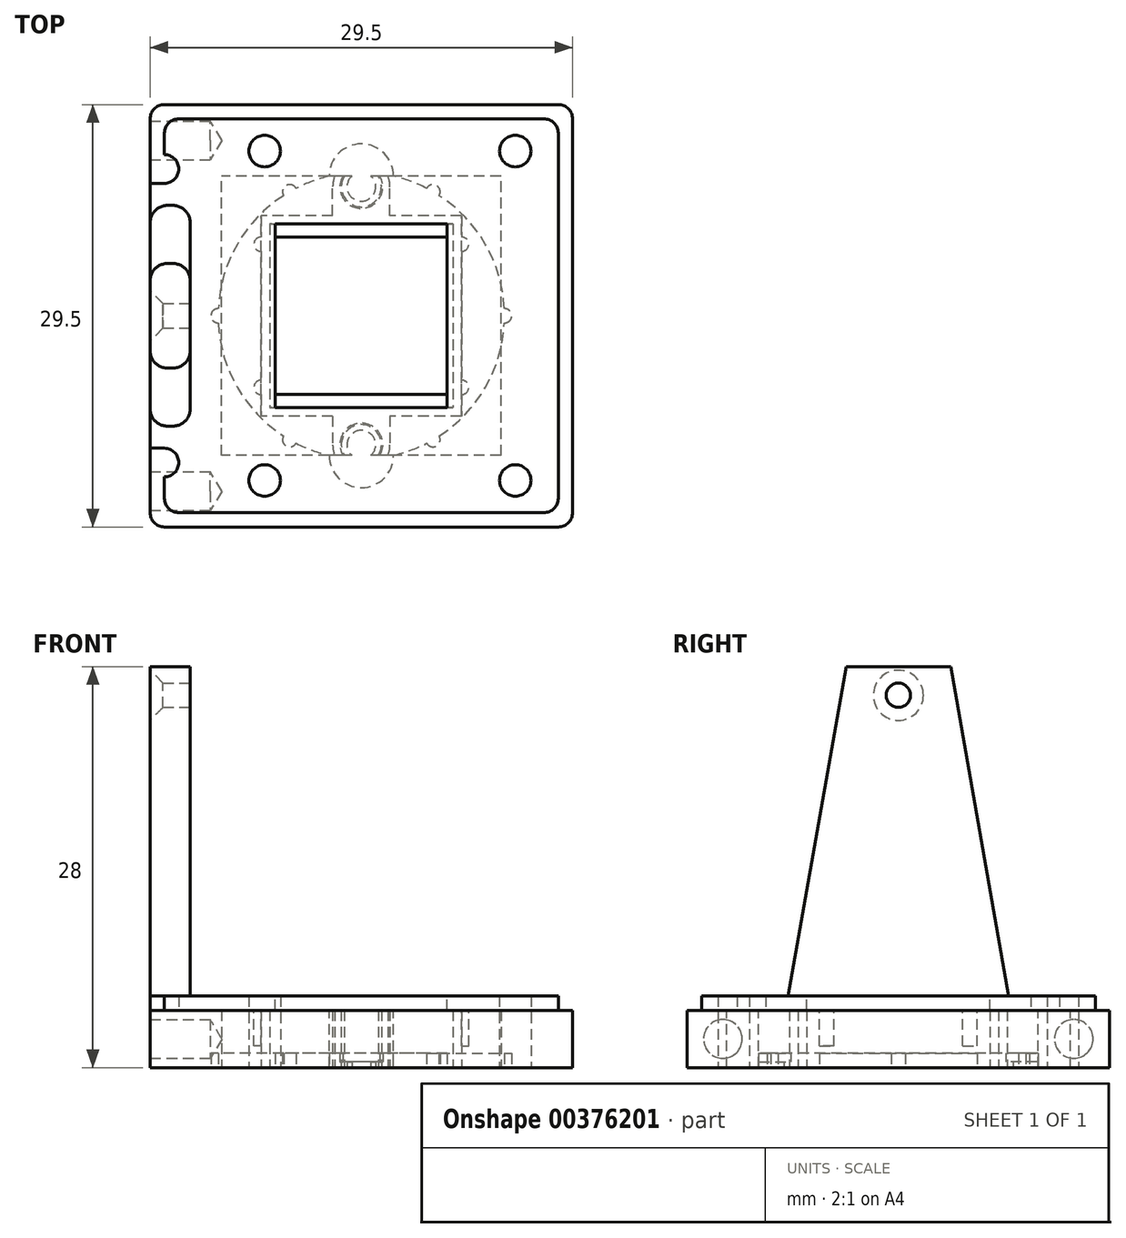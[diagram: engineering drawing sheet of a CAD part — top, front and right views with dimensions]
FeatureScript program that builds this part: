
annotation { "Feature Type Name" : "Feature", "Feature Type Description" : "" }
export const myFeature = defineFeature(function(context is Context, id is Id, definition is map)
    precondition{}
    {
        {
            var Q0;
            Q0=qCreatedBy(makeId("Top.planeOp"),FACE);
            var sketch = newSketch(context, id + "F0", { "sketchPlane" : qUnion([Q0])});
            skLineSegment(sketch, "E0.bottom", {"start": v(14.75, -14.75) * mm, "end": v(-14.75, -14.75) * mm});
            skLineSegment(sketch, "E0.top", {"start": v(14.75, 14.75) * mm, "end": v(-14.75, 14.75) * mm});
            skLineSegment(sketch, "E0.left", {"start": v(14.75, -14.75) * mm, "end": v(14.75, 14.75) * mm});
            skLineSegment(sketch, "E0.right", {"start": v(-14.75, -14.75) * mm, "end": v(-14.75, 14.75) * mm});
            skPoint(sketch, "E0.middle", {"position": v(0, 0) * mm});
            skLineSegment(sketch, "E1.0", {"start": v(-9.75, -9.75) * mm, "end": v(-9.75, 9.75) * mm});
            skLineSegment(sketch, "E1.1", {"start": v(9.75, -9.75) * mm, "end": v(-9.75, -9.75) * mm});
            skLineSegment(sketch, "E1.2", {"start": v(9.75, -9.75) * mm, "end": v(9.75, 9.75) * mm});
            skLineSegment(sketch, "E1.3", {"start": v(9.75, 9.75) * mm, "end": v(-9.75, 9.75) * mm});
            skSolve(sketch);
        }
        {
            var Q0;
            Q0=qSketchRegion(id+"F0",true);
            extrude(context, id + "F1", {"entities" : qUnion([Q0]), "depth" : 4 * mm, "offsetDistance" : 25 * mm});
        }
        {
            var Q0;
            Q0=makeQuery(id+"F1.opExtrude","CAP_FACE",FACE,{"disambiguationData":[OSD([sQuery(id+"F0.wireOp",EDGE,"E0.bottom"),sQuery(id+"F0.wireOp",EDGE,"E0.top"),sQuery(id+"F0.wireOp",EDGE,"E0.left"),sQuery(id+"F0.wireOp",EDGE,"E0.right"),sQuery(id+"F0.wireOp",EDGE,"E1.0"),sQuery(id+"F0.wireOp",EDGE,"E1.1"),sQuery(id+"F0.wireOp",EDGE,"E1.2"),sQuery(id+"F0.wireOp",EDGE,"E1.3")])],"isStart":false});
            var sketch = newSketch(context, id + "F2", { "sketchPlane" : qUnion([Q0])});
            skLineSegment(sketch, "E2.0", {"start": v(13.75, 13.75) * mm, "end": v(-13.75, 13.75) * mm});
            skLineSegment(sketch, "E2.1", {"start": v(13.75, -13.75) * mm, "end": v(13.75, 13.75) * mm});
            skLineSegment(sketch, "E2.2", {"start": v(13.75, -13.75) * mm, "end": v(-13.75, -13.75) * mm});
            skLineSegment(sketch, "E2.3", {"start": v(-13.75, -13.75) * mm, "end": v(-13.75, -11.25) * mm});
            skLineSegment(sketch, "E3.bottom", {"start": v(-14.75, -8.65) * mm, "end": v(-11.95, -8.65) * mm});
            skLineSegment(sketch, "E3.top", {"start": v(-14.75, 8.65) * mm, "end": v(-11.95, 8.65) * mm});
            skLineSegment(sketch, "E3.left", {"start": v(-14.75, -8.65) * mm, "end": v(-14.75, 8.65) * mm});
            skLineSegment(sketch, "E3.right", {"start": v(-11.95, -8.65) * mm, "end": v(-11.95, 8.65) * mm});
            skPoint(sketch, "E3.middle", {"position": v(-13.35, 0) * mm});
            skPoint(sketch, "E3.middle.positionSnap0", {"position": v(-13.75, 0) * mm});
            skPoint(sketch, "E3.centerSnap0", {"position": v(-13.75, 0) * mm});
            skLineSegment(sketch, "E4.trimOffspring", {"start": v(-13.75, 11.25) * mm, "end": v(-13.75, 13.75) * mm});
            skArc(sketch, "E5", {"start": v(-13.75, 9.25) * mm, "mid": v(-12.75, 10.25) * mm, "end": v(-13.75, 11.25) * mm});
            skArc(sketch, "E6", {"start": v(-13.75, -11.25) * mm, "mid": v(-12.75, -10.25) * mm, "end": v(-13.75, -9.25) * mm});
            skLineSegment(sketch, "E7", {"start": v(-13.75, -9.25) * mm, "end": v(-14.75, -9.25) * mm});
            skLineSegment(sketch, "E8", {"start": v(-13.75, 9.25) * mm, "end": v(-14.75, 9.25) * mm});
            skCircle(sketch, "E9", {"center": v(0, 9.75) * mm, "radius": 2.25 * mm});
            skCircle(sketch, "E10", {"center": v(0, -9.75) * mm, "radius": 2.25 * mm});
            skCircle(sketch, "E11", {"center": v(0, 9.75) * mm, "radius": 1.25 * mm, "construction": true});
            skCircle(sketch, "E12", {"center": v(0, -9.75) * mm, "radius": 1.25 * mm, "construction": true});
            skLineSegment(sketch, "E13", {"start": v(-13.35, 0) * mm, "end": v(0, 0) * mm, "construction": true});
            skLineSegment(sketch, "E14.bottom", {"start": v(6, -7) * mm, "end": v(-6, -7) * mm});
            skLineSegment(sketch, "E14.top", {"start": v(6, 7) * mm, "end": v(-6, 7) * mm});
            skLineSegment(sketch, "E14.left", {"start": v(6, -7) * mm, "end": v(6, 7) * mm});
            skLineSegment(sketch, "E14.right", {"start": v(-6, -7) * mm, "end": v(-6, 7) * mm});
            skPoint(sketch, "E14.middle", {"position": v(0, 0) * mm});
            skSolve(sketch);
        }
        {
            var Q0;
            {var subQ5=sQuery(id+"F2.wireOp",EDGE,"E8");Q0=makeQuery(id+"F2.imprint","IMPRINT",FACE,{"disambiguationData":[TD([[makeQuery(id+"F2.imprint","IMPRINT",EDGE,{"derivedFrom":subQ5}),1.0]])]});}
            var Q1;
            {var subQ8=sQuery(id+"F2.wireOp",EDGE,"E2.0");Q1=makeQuery(id+"F2.imprint","IMPRINT",FACE,{"disambiguationData":[TD([[makeQuery(id+"F2.imprint","IMPRINT",EDGE,{"derivedFrom":subQ8}),1.0]])]});}
            var Q2;
            {var subQ3=sQuery(id+"F2.wireOp",EDGE,"E7");Q2=makeQuery(id+"F2.imprint","IMPRINT",FACE,{"disambiguationData":[TD([[makeQuery(id+"F2.imprint","IMPRINT",EDGE,{"derivedFrom":subQ3}),-1.0]])]});}
            var Q3;
            {var subQ3=sQuery(id+"F2.wireOp",EDGE,"E3.left");Q3=makeQuery(id+"F2.imprint","IMPRINT",FACE,{"disambiguationData":[TD([[makeQuery(id+"F2.imprint","IMPRINT",EDGE,{"derivedFrom":subQ3}),-1.0]])]});}
            var Q4;
            Q4=makeQuery(id+"F2.imprint","IMPRINT",FACE,{"disambiguationData":[TD([[makeQuery(id+"F2.imprint","IMPRINT",EDGE,{"derivedFrom":sQuery(id+"F2.wireOp",EDGE,"E14.bottom")}),1.0]])]});
            var Q5;
            {var subQ0=sQuery(id+"F2.wireOp",EDGE,"E9");var subQ1=makeQuery(id+"F1.opExtrude","CAP_EDGE",EDGE,{"disambiguationData":[OSD([sQuery(id+"F0.wireOp",EDGE,"E1.3")])],"isStart":false});var subQ2=makeQuery(id+"F2.imprint","INTERSECT",VERTEX,{"disambiguationData":[OD(0.0)],"derivedFrom":[subQ1,subQ0]});Q5=makeQuery(id+"F2.imprint","IMPRINT",FACE,{"disambiguationData":[TD([[makeQuery(id+"F2.imprint","IMPRINT",EDGE,{"disambiguationData":[TD([[subQ2,-1.0]])],"derivedFrom":subQ0}),1.0]])]});}
            var Q6;
            {var subQ0=sQuery(id+"F2.wireOp",EDGE,"E9");var subQ1=makeQuery(id+"F1.opExtrude","CAP_EDGE",EDGE,{"disambiguationData":[OSD([sQuery(id+"F0.wireOp",EDGE,"E1.3")])],"isStart":false});var subQ2=makeQuery(id+"F2.imprint","INTERSECT",VERTEX,{"disambiguationData":[OD(0.0)],"derivedFrom":[subQ1,subQ0]});Q6=makeQuery(id+"F2.imprint","IMPRINT",FACE,{"disambiguationData":[TD([[makeQuery(id+"F2.imprint","IMPRINT",EDGE,{"disambiguationData":[TD([[subQ2,1.0]])],"derivedFrom":subQ0}),1.0]])]});}
            var Q7;
            {var subQ0=sQuery(id+"F2.wireOp",EDGE,"E10");var subQ1=makeQuery(id+"F1.opExtrude","CAP_EDGE",EDGE,{"disambiguationData":[OSD([sQuery(id+"F0.wireOp",EDGE,"E1.1")])],"isStart":false});var subQ2=makeQuery(id+"F2.imprint","INTERSECT",VERTEX,{"disambiguationData":[OD(0.0)],"derivedFrom":[subQ1,subQ0]});Q7=makeQuery(id+"F2.imprint","IMPRINT",FACE,{"disambiguationData":[TD([[makeQuery(id+"F2.imprint","IMPRINT",EDGE,{"disambiguationData":[TD([[subQ2,-1.0]])],"derivedFrom":subQ0}),1.0]])]});}
            var Q8;
            {var subQ0=sQuery(id+"F2.wireOp",EDGE,"E10");var subQ1=makeQuery(id+"F1.opExtrude","CAP_EDGE",EDGE,{"disambiguationData":[OSD([sQuery(id+"F0.wireOp",EDGE,"E1.1")])],"isStart":false});var subQ2=makeQuery(id+"F2.imprint","INTERSECT",VERTEX,{"disambiguationData":[OD(0.0)],"derivedFrom":[subQ1,subQ0]});Q8=makeQuery(id+"F2.imprint","IMPRINT",FACE,{"disambiguationData":[TD([[makeQuery(id+"F2.imprint","IMPRINT",EDGE,{"disambiguationData":[TD([[subQ2,1.0]])],"derivedFrom":subQ0}),1.0]])]});}
            var Q9;
            {var subQ0=sQuery(id+"F2.wireOp",EDGE,"E12");var subQ1=makeQuery(id+"F1.opExtrude","CAP_EDGE",EDGE,{"disambiguationData":[OSD([sQuery(id+"F0.wireOp",EDGE,"E1.1")])],"isStart":false});var subQ2=makeQuery(id+"F2.imprint","INTERSECT",VERTEX,{"disambiguationData":[OD(0.0)],"derivedFrom":[subQ1,subQ0]});Q9=makeQuery(id+"F2.imprint","IMPRINT",FACE,{"disambiguationData":[TD([[makeQuery(id+"F2.imprint","IMPRINT",EDGE,{"disambiguationData":[TD([[subQ2,-1.0]])],"derivedFrom":subQ0}),1.0]])]});}
            var Q10;
            {var subQ0=sQuery(id+"F2.wireOp",EDGE,"E11");var subQ1=makeQuery(id+"F1.opExtrude","CAP_EDGE",EDGE,{"disambiguationData":[OSD([sQuery(id+"F0.wireOp",EDGE,"E1.3")])],"isStart":false});var subQ2=makeQuery(id+"F2.imprint","INTERSECT",VERTEX,{"disambiguationData":[OD(0.0)],"derivedFrom":[subQ1,subQ0]});Q10=makeQuery(id+"F2.imprint","IMPRINT",FACE,{"disambiguationData":[TD([[makeQuery(id+"F2.imprint","IMPRINT",EDGE,{"disambiguationData":[TD([[subQ2,-1.0]])],"derivedFrom":subQ0}),1.0]])]});}
            var Q11;
            {var subQ0=sQuery(id+"F2.wireOp",EDGE,"E11");var subQ1=makeQuery(id+"F1.opExtrude","CAP_EDGE",EDGE,{"disambiguationData":[OSD([sQuery(id+"F0.wireOp",EDGE,"E1.3")])],"isStart":false});var subQ2=makeQuery(id+"F2.imprint","INTERSECT",VERTEX,{"disambiguationData":[OD(0.0)],"derivedFrom":[subQ1,subQ0]});Q11=makeQuery(id+"F2.imprint","IMPRINT",FACE,{"disambiguationData":[TD([[makeQuery(id+"F2.imprint","IMPRINT",EDGE,{"disambiguationData":[TD([[subQ2,1.0]])],"derivedFrom":subQ0}),1.0]])]});}
            var Q12;
            {var subQ0=sQuery(id+"F2.wireOp",EDGE,"E12");var subQ1=makeQuery(id+"F1.opExtrude","CAP_EDGE",EDGE,{"disambiguationData":[OSD([sQuery(id+"F0.wireOp",EDGE,"E1.1")])],"isStart":false});var subQ2=makeQuery(id+"F2.imprint","INTERSECT",VERTEX,{"disambiguationData":[OD(0.0)],"derivedFrom":[subQ1,subQ0]});Q12=makeQuery(id+"F2.imprint","IMPRINT",FACE,{"disambiguationData":[TD([[makeQuery(id+"F2.imprint","IMPRINT",EDGE,{"disambiguationData":[TD([[subQ2,1.0]])],"derivedFrom":subQ0}),1.0]])]});}
            extrude(context, id + "F3", {"entities" : qUnion([Q0, Q1, Q2, Q3, Q4, Q5, Q6, Q7, Q8, Q9, Q10, Q11, Q12]), "operationType" : NewBodyOperationType.ADD, "depth" : 1 * mm, "offsetDistance" : 25 * mm});
        }
        {
            var Q0;
            {var subQ5=sQuery(id+"F2.wireOp",EDGE,"E3.left");Q0=makeQuery(id+"F2.imprint","IMPRINT",FACE,{"disambiguationData":[TD([[makeQuery(id+"F2.imprint","IMPRINT",EDGE,{"derivedFrom":subQ5}),-1.0]])]});}
            var Q1;
            {var subQ5=sQuery(id+"F2.wireOp",EDGE,"E3.right");Q1=makeQuery(id+"F2.imprint","IMPRINT",FACE,{"disambiguationData":[TD([[makeQuery(id+"F2.imprint","IMPRINT",EDGE,{"derivedFrom":subQ5}),1.0]])]});}
            extrude(context, id + "F4", {"entities" : qUnion([Q0, Q1]), "operationType" : NewBodyOperationType.ADD, "depth" : 24 * mm, "offsetDistance" : 25 * mm});
        }
        {
            var Q0;
            Q0=makeQuery(id+"F4.opExtrude","CAP_EDGE",EDGE,{"disambiguationData":[OSD([sQuery(id+"F2.wireOp",EDGE,"E3.bottom")])],"isStart":false});
            var Q1;
            Q1=makeQuery(id+"F4.opExtrude","CAP_EDGE",EDGE,{"disambiguationData":[OSD([sQuery(id+"F2.wireOp",EDGE,"E3.top")])],"isStart":false});
            chamfer(context, id + "F5", {"entities" : qUnion([Q0, Q1]), "chamferType" : ChamferType.OFFSET_ANGLE, "width" : 5 * mm, "oppositeDirection" : false, "angle" : 80 * degree, "tangentPropagation" : true});
        }
        {
            var Q0;
            Q0=makeQuery(id+"F5.opChamfer","BLEND_EDGE",EDGE,{"blendedFrom":[makeQuery(id+"F4.opExtrude","CAP_EDGE",EDGE,{"disambiguationData":[OSD([sQuery(id+"F2.wireOp",EDGE,"E3.bottom")])],"isStart":false}),makeQuery(id+"F4.opExtrude","SWEPT_FACE",FACE,{"disambiguationData":[OSD([sQuery(id+"F2.wireOp",EDGE,"E3.right")])]})],"blendedInto":[makeQuery(id+"F4.opExtrude","SWEPT_FACE",FACE,{"disambiguationData":[OSD([sQuery(id+"F2.wireOp",EDGE,"E3.right")])]})]});
            var Q1;
            Q1=makeQuery(id+"F5.opChamfer","BLEND_EDGE",EDGE,{"blendedFrom":[makeQuery(id+"F4.opExtrude","CAP_EDGE",EDGE,{"disambiguationData":[OSD([sQuery(id+"F2.wireOp",EDGE,"E3.bottom")])],"isStart":false}),makeQuery(id+"F4.boolean.opBoolean","MERGE",FACE,{"derivedFrom":[makeQuery(id+"F1.opExtrude","SWEPT_FACE",FACE,{"disambiguationData":[OSD([sQuery(id+"F0.wireOp",EDGE,"E0.right")])]}),makeQuery(id+"F4.opExtrude","SWEPT_FACE",FACE,{"disambiguationData":[OSD([sQuery(id+"F2.wireOp",EDGE,"E3.left")])]})]})],"blendedInto":[makeQuery(id+"F4.boolean.opBoolean","MERGE",FACE,{"derivedFrom":[makeQuery(id+"F1.opExtrude","SWEPT_FACE",FACE,{"disambiguationData":[OSD([sQuery(id+"F0.wireOp",EDGE,"E0.right")])]}),makeQuery(id+"F4.opExtrude","SWEPT_FACE",FACE,{"disambiguationData":[OSD([sQuery(id+"F2.wireOp",EDGE,"E3.left")])]})]})]});
            var Q2;
            Q2=makeQuery(id+"F5.opChamfer","BLEND_EDGE",EDGE,{"blendedFrom":[makeQuery(id+"F4.opExtrude","CAP_EDGE",EDGE,{"disambiguationData":[OSD([sQuery(id+"F2.wireOp",EDGE,"E3.top")])],"isStart":false}),makeQuery(id+"F4.opExtrude","SWEPT_FACE",FACE,{"disambiguationData":[OSD([sQuery(id+"F2.wireOp",EDGE,"E3.right")])]})],"blendedInto":[makeQuery(id+"F4.opExtrude","SWEPT_FACE",FACE,{"disambiguationData":[OSD([sQuery(id+"F2.wireOp",EDGE,"E3.right")])]})]});
            var Q3;
            Q3=makeQuery(id+"F5.opChamfer","BLEND_EDGE",EDGE,{"blendedFrom":[makeQuery(id+"F4.opExtrude","CAP_EDGE",EDGE,{"disambiguationData":[OSD([sQuery(id+"F2.wireOp",EDGE,"E3.top")])],"isStart":false}),makeQuery(id+"F4.boolean.opBoolean","MERGE",FACE,{"derivedFrom":[makeQuery(id+"F1.opExtrude","SWEPT_FACE",FACE,{"disambiguationData":[OSD([sQuery(id+"F0.wireOp",EDGE,"E0.right")])]}),makeQuery(id+"F4.opExtrude","SWEPT_FACE",FACE,{"disambiguationData":[OSD([sQuery(id+"F2.wireOp",EDGE,"E3.left")])]})]})],"blendedInto":[makeQuery(id+"F4.boolean.opBoolean","MERGE",FACE,{"derivedFrom":[makeQuery(id+"F1.opExtrude","SWEPT_FACE",FACE,{"disambiguationData":[OSD([sQuery(id+"F0.wireOp",EDGE,"E0.right")])]}),makeQuery(id+"F4.opExtrude","SWEPT_FACE",FACE,{"disambiguationData":[OSD([sQuery(id+"F2.wireOp",EDGE,"E3.left")])]})]})]});
            fillet(context, id + "F6", {"entities" : qUnion([Q0, Q1, Q2, Q3]), "radius" : 1.2 * mm, "tangentPropagation" : true, "allowEdgeOverflow" : false});
        }
        {
            var Q0;
            Q0=makeQuery(id+"F3.opExtrude","CAP_FACE",FACE,{"disambiguationData":[OSD([sQuery(id+"F0.wireOp",EDGE,"E0.right"),sQuery(id+"F0.wireOp",EDGE,"E1.0"),sQuery(id+"F0.wireOp",EDGE,"E1.1"),sQuery(id+"F0.wireOp",EDGE,"E1.2"),sQuery(id+"F0.wireOp",EDGE,"E1.3"),sQuery(id+"F2.wireOp",EDGE,"E2.0"),sQuery(id+"F2.wireOp",EDGE,"E2.1"),sQuery(id+"F2.wireOp",EDGE,"E2.2"),sQuery(id+"F2.wireOp",EDGE,"E2.3"),sQuery(id+"F2.wireOp",EDGE,"E3.left"),sQuery(id+"F2.wireOp",EDGE,"E4.trimOffspring"),sQuery(id+"F2.wireOp",EDGE,"E5"),sQuery(id+"F2.wireOp",EDGE,"E6"),sQuery(id+"F2.wireOp",EDGE,"E7"),sQuery(id+"F2.wireOp",EDGE,"E8"),sQuery(id+"F2.wireOp",EDGE,"E9"),sQuery(id+"F2.wireOp",EDGE,"E10")])],"isStart":false});
            var sketch = newSketch(context, id + "F7", { "sketchPlane" : qUnion([Q0])});
            skCircle(sketch, "E15", {"center": v(10.75, 11.5) * mm, "radius": 1.19 * mm});
            skCircle(sketch, "E16", {"center": v(10.75, -11.5) * mm, "radius": 1.19 * mm});
            skCircle(sketch, "E17", {"center": v(-6.75, 11.5) * mm, "radius": 1.4 * mm});
            skCircle(sketch, "E18", {"center": v(-6.75, -11.5) * mm, "radius": 1.2 * mm});
            skLineSegment(sketch, "E19", {"start": v(0, 0) * mm, "end": v(6.78, 0) * mm, "construction": true});
            skCircle(sketch, "E20", {"center": v(0, -9) * mm, "radius": 0.9 * mm});
            skCircle(sketch, "E21", {"center": v(0, 9) * mm, "radius": 2.16 * mm});
            skSolve(sketch);
        }
        {
            var Q0;
            Q0=sQuery(id+"F7.wireOp",VERTEX,"E15.center");
            var Q1;
            Q1=sQuery(id+"F7.wireOp",VERTEX,"E16.center");
            var Q2;
            Q2=sQuery(id+"F7.wireOp",VERTEX,"E17.center");
            var Q3;
            Q3=sQuery(id+"F7.wireOp",VERTEX,"E18.center");
            var Q4;
            Q4=makeQuery(id+"F1.opExtrude","SWEPT_BODY",BODY,{"disambiguationData":[OSD([sQuery(id+"F0.wireOp",EDGE,"E0.bottom"),sQuery(id+"F0.wireOp",EDGE,"E0.top"),sQuery(id+"F0.wireOp",EDGE,"E0.left"),sQuery(id+"F0.wireOp",EDGE,"E0.right"),sQuery(id+"F0.wireOp",EDGE,"E1.0"),sQuery(id+"F0.wireOp",EDGE,"E1.1"),sQuery(id+"F0.wireOp",EDGE,"E1.2"),sQuery(id+"F0.wireOp",EDGE,"E1.3")])]});
            hole(context, id + "F8", {"style" : HoleStyle.SIMPLE, "endStyle" : HoleEndStyle.BLIND, "holeDiameter" : 2.2 * mm, "majorDiameter" : 5 * mm, "holeDepth" : 20 * mm, "isTappedThrough" : true, "tappedDepth" : 12 * mm, "tapClearance" : 3, "locations" : qUnion([Q0, Q1, Q2, Q3]), "scope" : qUnion([Q4])});
        }
        {
            var Q0;
            Q0=qCreatedBy(makeId("Top.planeOp"),FACE);
            var sketch = newSketch(context, id + "F9", { "sketchPlane" : qUnion([Q0])});
            skCircle(sketch, "E22", {"center": v(0, 0) * mm, "radius": 10 * mm});
            skLineSegment(sketch, "E23.bottom", {"start": v(6, -5.5) * mm, "end": v(-6, -5.5) * mm});
            skLineSegment(sketch, "E23.top", {"start": v(6, 5.5) * mm, "end": v(-6, 5.5) * mm});
            skLineSegment(sketch, "E23.left", {"start": v(6, -5.5) * mm, "end": v(6, 5.5) * mm});
            skLineSegment(sketch, "E23.right", {"start": v(-6, -5.5) * mm, "end": v(-6, 5.5) * mm});
            skCircle(sketch, "E24", {"center": v(0, 10) * mm, "radius": 2 * mm});
            skCircle(sketch, "E25", {"center": v(0, -10) * mm, "radius": 2 * mm});
            skCircle(sketch, "E26", {"center": v(10, 0) * mm, "radius": 0.5 * mm});
            skCircle(sketch, "E27.1.0", {"center": v(5, 8.66) * mm, "radius": 0.5 * mm});
            skCircle(sketch, "E27.2.0", {"center": v(-5, 8.66) * mm, "radius": 0.5 * mm});
            skCircle(sketch, "E28.1.3.0", {"center": v(-10, 0) * mm, "radius": 0.5 * mm});
            skCircle(sketch, "E28.1.4.0", {"center": v(-5, -8.66) * mm, "radius": 0.5 * mm});
            skCircle(sketch, "E28.1.5.0", {"center": v(5, -8.66) * mm, "radius": 0.5 * mm});
            skSolve(sketch);
        }
        {
            var Q0;
            Q0=qSketchRegion(id+"F9",true);
            var Q1;
            {var subQ0=sQuery(id+"F9.wireOp",EDGE,"nrrdsNW8-0lje-5FPb-w1w5-OaGebltPMd51");var subQ1=sQuery(id+"F9.wireOp",EDGE,"E22");var subQ2=makeQuery(id+"F9.imprint","INTERSECT",VERTEX,{"disambiguationData":[OD(0.0)],"derivedFrom":[subQ1,subQ0]});Q1=makeQuery(id+"F9.imprint","IMPRINT",FACE,{"disambiguationData":[TD([[makeQuery(id+"F9.imprint","IMPRINT",EDGE,{"disambiguationData":[TD([[subQ2,-1.0]])],"derivedFrom":subQ1}),1.0]])]});}
            var Q2;
            {var subQ0=sQuery(id+"F9.wireOp",EDGE,"nrrdsNW8-0lje-5FPb-w1w5-OaGebltPMd51");var subQ1=sQuery(id+"F9.wireOp",EDGE,"E22");var subQ2=makeQuery(id+"F9.imprint","INTERSECT",VERTEX,{"disambiguationData":[OD(0.0)],"derivedFrom":[subQ1,subQ0]});Q2=makeQuery(id+"F9.imprint","IMPRINT",FACE,{"disambiguationData":[TD([[makeQuery(id+"F9.imprint","IMPRINT",EDGE,{"disambiguationData":[TD([[subQ2,-1.0]])],"derivedFrom":subQ1}),-1.0]])]});}
            var Q3;
            {var subQ0=sQuery(id+"F9.wireOp",EDGE,"nrrdsNW8-0lje-5FPb-w1w5-OaGebltPMd51");var subQ1=sQuery(id+"F9.wireOp",EDGE,"E24");var subQ2=makeQuery(id+"F9.imprint","INTERSECT",VERTEX,{"disambiguationData":[OD(0.0)],"derivedFrom":[subQ1,subQ0]});Q3=makeQuery(id+"F9.imprint","IMPRINT",FACE,{"disambiguationData":[TD([[makeQuery(id+"F9.imprint","IMPRINT",EDGE,{"disambiguationData":[TD([[subQ2,-1.0]])],"derivedFrom":subQ1}),-1.0]])]});}
            var Q4;
            {var subQ0=sQuery(id+"F9.wireOp",EDGE,"S1DDepDF-IZdj-yKmF-IfUE-yXN7PUjpcanx");var subQ1=sQuery(id+"F9.wireOp",EDGE,"E22");var subQ2=makeQuery(id+"F9.imprint","INTERSECT",VERTEX,{"disambiguationData":[OD(0.0)],"derivedFrom":[subQ1,subQ0]});Q4=makeQuery(id+"F9.imprint","IMPRINT",FACE,{"disambiguationData":[TD([[makeQuery(id+"F9.imprint","IMPRINT",EDGE,{"disambiguationData":[TD([[subQ2,-1.0]])],"derivedFrom":subQ1}),1.0]])]});}
            var Q5;
            {var subQ0=sQuery(id+"F9.wireOp",EDGE,"S1DDepDF-IZdj-yKmF-IfUE-yXN7PUjpcanx");var subQ1=sQuery(id+"F9.wireOp",EDGE,"E25");var subQ2=makeQuery(id+"F9.imprint","INTERSECT",VERTEX,{"disambiguationData":[OD(0.0)],"derivedFrom":[subQ1,subQ0]});Q5=makeQuery(id+"F9.imprint","IMPRINT",FACE,{"disambiguationData":[TD([[makeQuery(id+"F9.imprint","IMPRINT",EDGE,{"disambiguationData":[TD([[subQ2,-1.0]])],"derivedFrom":subQ1}),-1.0]])]});}
            var Q6;
            {var subQ0=sQuery(id+"F9.wireOp",EDGE,"S1DDepDF-IZdj-yKmF-IfUE-yXN7PUjpcanx");var subQ1=sQuery(id+"F9.wireOp",EDGE,"E22");var subQ2=makeQuery(id+"F9.imprint","INTERSECT",VERTEX,{"disambiguationData":[OD(0.0)],"derivedFrom":[subQ1,subQ0]});Q6=makeQuery(id+"F9.imprint","IMPRINT",FACE,{"disambiguationData":[TD([[makeQuery(id+"F9.imprint","IMPRINT",EDGE,{"disambiguationData":[TD([[subQ2,-1.0]])],"derivedFrom":subQ1}),-1.0]])]});}
            extrude(context, id + "F10", {"entities" : qUnion([Q0, Q1, Q2, Q3, Q4, Q5, Q6]), "depth" : 1 * mm, "offsetDistance" : 25 * mm});
        }
        {
            var Q0;
            Q0=qCreatedBy(makeId("Top.planeOp"),FACE);
            var sketch = newSketch(context, id + "F11", { "sketchPlane" : qUnion([Q0])});
            skLineSegment(sketch, "E29.bottom", {"start": v(7, -7) * mm, "end": v(-7, -7) * mm});
            skLineSegment(sketch, "E29.top", {"start": v(7, 7) * mm, "end": v(-7, 7) * mm});
            skLineSegment(sketch, "E29.left", {"start": v(7, -7) * mm, "end": v(7, 7) * mm});
            skLineSegment(sketch, "E29.right", {"start": v(-7, -7) * mm, "end": v(-7, 7) * mm});
            skPoint(sketch, "E29.middle", {"position": v(0, 0) * mm});
            skLineSegment(sketch, "E30.0", {"start": v(6.4, 6.4) * mm, "end": v(-6.4, 6.4) * mm});
            skLineSegment(sketch, "E30.1", {"start": v(6.4, -6.4) * mm, "end": v(6.4, 6.4) * mm});
            skLineSegment(sketch, "E30.2", {"start": v(6.4, -6.4) * mm, "end": v(-6.4, -6.4) * mm});
            skLineSegment(sketch, "E30.3", {"start": v(-6.4, -6.4) * mm, "end": v(-6.4, 6.4) * mm});
            skCircle(sketch, "E31", {"center": v(0, 9) * mm, "radius": 2 * mm});
            skPoint(sketch, "E31.centerSnap0", {"position": v(0, 7) * mm});
            skCircle(sketch, "E32.0", {"center": v(0, 9) * mm, "radius": 1.4 * mm});
            skCircle(sketch, "E33", {"center": v(0, -9) * mm, "radius": 2 * mm});
            skPoint(sketch, "E33.centerSnap0", {"position": v(0, -7) * mm});
            skCircle(sketch, "E34.0", {"center": v(0, -9) * mm, "radius": 1.4 * mm});
            skLineSegment(sketch, "E35", {"start": v(-2.78, 9) * mm, "end": v(3.33, 9) * mm, "construction": true});
            skLineSegment(sketch, "E36", {"start": v(-2.82, -9) * mm, "end": v(3.88, -9) * mm, "construction": true});
            skLineSegment(sketch, "E37", {"start": v(-2, 9) * mm, "end": v(-2, 7) * mm});
            skLineSegment(sketch, "E38", {"start": v(2, 9) * mm, "end": v(2, 7) * mm});
            skLineSegment(sketch, "E39", {"start": v(-2, -9) * mm, "end": v(-2, -7) * mm});
            skLineSegment(sketch, "E40", {"start": v(2, -9) * mm, "end": v(2, -7) * mm});
            skSolve(sketch);
        }
        {
            var Q0;
            {var subQ0=sQuery(id+"F11.wireOp",EDGE,"E37");Q0=makeQuery(id+"F11.imprint","IMPRINT",FACE,{"disambiguationData":[TD([[makeQuery(id+"F11.imprint","IMPRINT",EDGE,{"derivedFrom":subQ0}),1.0]])]});}
            var Q1;
            Q1=makeQuery(id+"F11.imprint","IMPRINT",FACE,{"disambiguationData":[TD([[makeQuery(id+"F11.imprint","IMPRINT",EDGE,{"derivedFrom":sQuery(id+"F11.wireOp",EDGE,"E32.0")}),-1.0]])]});
            var Q2;
            {var subQ0=sQuery(id+"F11.wireOp",EDGE,"E38");Q2=makeQuery(id+"F11.imprint","IMPRINT",FACE,{"disambiguationData":[TD([[makeQuery(id+"F11.imprint","IMPRINT",EDGE,{"derivedFrom":subQ0}),-1.0]])]});}
            var Q3;
            {var subQ1=sQuery(id+"F11.wireOp",EDGE,"E29.left");Q3=makeQuery(id+"F11.imprint","IMPRINT",FACE,{"disambiguationData":[TD([[makeQuery(id+"F11.imprint","IMPRINT",EDGE,{"derivedFrom":subQ1}),1.0]])]});}
            var Q4;
            {var subQ0=sQuery(id+"F11.wireOp",EDGE,"E40");Q4=makeQuery(id+"F11.imprint","IMPRINT",FACE,{"disambiguationData":[TD([[makeQuery(id+"F11.imprint","IMPRINT",EDGE,{"derivedFrom":subQ0}),1.0]])]});}
            var Q5;
            Q5=makeQuery(id+"F11.imprint","IMPRINT",FACE,{"disambiguationData":[TD([[makeQuery(id+"F11.imprint","IMPRINT",EDGE,{"derivedFrom":sQuery(id+"F11.wireOp",EDGE,"E34.0")}),-1.0]])]});
            var Q6;
            {var subQ0=sQuery(id+"F11.wireOp",EDGE,"E39");Q6=makeQuery(id+"F11.imprint","IMPRINT",FACE,{"disambiguationData":[TD([[makeQuery(id+"F11.imprint","IMPRINT",EDGE,{"derivedFrom":subQ0}),-1.0]])]});}
            extrude(context, id + "F12", {"entities" : qUnion([Q0, Q1, Q2, Q3, Q4, Q5, Q6]), "depth" : 5 * mm, "offsetDistance" : 25 * mm});
        }
        {
            var Q0;
            {var subQ0=sQuery(id+"F2.wireOp",EDGE,"E3.left");var subQ1=sQuery(id+"F0.wireOp",EDGE,"E0.right");Q0=makeQuery(id+"F3.boolean.opBoolean","MERGE",FACE,{"derivedFrom":[makeQuery(id+"F4.boolean.opBoolean","MERGE",FACE,{"derivedFrom":[makeQuery(id+"F1.opExtrude","SWEPT_FACE",FACE,{"disambiguationData":[OSD([subQ1])]}),makeQuery(id+"F4.opExtrude","SWEPT_FACE",FACE,{"disambiguationData":[OSD([subQ0])]})]}),makeQuery(id+"F3.opExtrude","SWEPT_FACE",FACE,{"disambiguationData":[OSD([subQ1,subQ0])]})]});}
            var sketch = newSketch(context, id + "F13", { "sketchPlane" : qUnion([Q0])});
            skCircle(sketch, "E41", {"center": v(0, 26) * mm, "radius": 0.1 * mm});
            skCircle(sketch, "E42", {"center": v(-12.25, 2) * mm, "radius": 1.3 * mm});
            skPoint(sketch, "E42.centerSnap0", {"position": v(-14.75, 2) * mm});
            skCircle(sketch, "E43", {"center": v(12.25, 2) * mm, "radius": 1.3 * mm});
            skPoint(sketch, "E43.centerSnap0", {"position": v(14.75, 2) * mm});
            skSolve(sketch);
        }
        {
            var Q0;
            Q0=sQuery(id+"F13.wireOp",VERTEX,"E41.center");
            var Q1;
            Q1=makeQuery(id+"F1.opExtrude","SWEPT_BODY",BODY,{"disambiguationData":[OSD([sQuery(id+"F0.wireOp",EDGE,"E0.bottom"),sQuery(id+"F0.wireOp",EDGE,"E0.top"),sQuery(id+"F0.wireOp",EDGE,"E0.left"),sQuery(id+"F0.wireOp",EDGE,"E0.right"),sQuery(id+"F0.wireOp",EDGE,"E1.0"),sQuery(id+"F0.wireOp",EDGE,"E1.1"),sQuery(id+"F0.wireOp",EDGE,"E1.2"),sQuery(id+"F0.wireOp",EDGE,"E1.3")])]});
            hole(context, id + "F14", {"style" : HoleStyle.C_SINK, "endStyle" : HoleEndStyle.BLIND, "holeDiameter" : 1.7 * mm, "cSinkDiameter" : 3.5 * mm, "cSinkAngle" : 90 * degree, "majorDiameter" : 5 * mm, "holeDepth" : 5 * mm, "isTappedThrough" : true, "tappedDepth" : 12 * mm, "tapClearance" : 3, "locations" : qUnion([Q0]), "scope" : qUnion([Q1])});
        }
        {
            var Q0;
            Q0=sQuery(id+"F13.wireOp",VERTEX,"E42.center");
            var Q1;
            Q1=sQuery(id+"F13.wireOp",VERTEX,"E43.center");
            var Q2;
            Q2=makeQuery(id+"F1.opExtrude","SWEPT_BODY",BODY,{"disambiguationData":[OSD([sQuery(id+"F0.wireOp",EDGE,"E0.bottom"),sQuery(id+"F0.wireOp",EDGE,"E0.top"),sQuery(id+"F0.wireOp",EDGE,"E0.left"),sQuery(id+"F0.wireOp",EDGE,"E0.right"),sQuery(id+"F0.wireOp",EDGE,"E1.0"),sQuery(id+"F0.wireOp",EDGE,"E1.1"),sQuery(id+"F0.wireOp",EDGE,"E1.2"),sQuery(id+"F0.wireOp",EDGE,"E1.3")])]});
            hole(context, id + "F15", {"style" : HoleStyle.SIMPLE, "endStyle" : HoleEndStyle.BLIND, "holeDiameter" : 2.7 * mm, "majorDiameter" : 5 * mm, "holeDepth" : 4.2 * mm, "isTappedThrough" : true, "tappedDepth" : 12 * mm, "tapClearance" : 3, "locations" : qUnion([Q0, Q1]), "scope" : qUnion([Q2])});
        }
        {
            var Q0;
            Q0=makeQuery(id+"F10.opExtrude","CAP_FACE",FACE,{"disambiguationData":[OSD([sQuery(id+"F9.wireOp",EDGE,"E22"),sQuery(id+"F9.wireOp",EDGE,"E23.bottom"),sQuery(id+"F9.wireOp",EDGE,"E23.top"),sQuery(id+"F9.wireOp",EDGE,"E23.left"),sQuery(id+"F9.wireOp",EDGE,"E23.right"),sQuery(id+"F9.wireOp",EDGE,"E24"),sQuery(id+"F9.wireOp",EDGE,"E25"),sQuery(id+"F9.wireOp",EDGE,"E26"),sQuery(id+"F9.wireOp",EDGE,"E27.1.0"),sQuery(id+"F9.wireOp",EDGE,"E27.2.0"),sQuery(id+"F9.wireOp",EDGE,"E28.1.3.0"),sQuery(id+"F9.wireOp",EDGE,"E28.1.4.0"),sQuery(id+"F9.wireOp",EDGE,"E28.1.5.0")])],"isStart":false});
            var sketch = newSketch(context, id + "F16", { "sketchPlane" : qUnion([Q0])});
            skCircle(sketch, "E44", {"center": v(0, 9) * mm, "radius": 0.98 * mm});
            skCircle(sketch, "E45", {"center": v(0, -9) * mm, "radius": 1.12 * mm});
            skSolve(sketch);
        }
        {
            var Q0;
            Q0=sQuery(id+"F16.wireOp",VERTEX,"E44.center");
            var Q1;
            Q1=sQuery(id+"F16.wireOp",VERTEX,"E45.center");
            var Q2;
            Q2=makeQuery(id+"F10.opExtrude","SWEPT_BODY",BODY,{"disambiguationData":[OSD([sQuery(id+"F9.wireOp",EDGE,"E22"),sQuery(id+"F9.wireOp",EDGE,"E23.bottom"),sQuery(id+"F9.wireOp",EDGE,"E23.top"),sQuery(id+"F9.wireOp",EDGE,"E23.left"),sQuery(id+"F9.wireOp",EDGE,"E23.right"),sQuery(id+"F9.wireOp",EDGE,"E24"),sQuery(id+"F9.wireOp",EDGE,"E25"),sQuery(id+"F9.wireOp",EDGE,"E26"),sQuery(id+"F9.wireOp",EDGE,"E27.1.0"),sQuery(id+"F9.wireOp",EDGE,"E27.2.0"),sQuery(id+"F9.wireOp",EDGE,"E28.1.3.0"),sQuery(id+"F9.wireOp",EDGE,"E28.1.4.0"),sQuery(id+"F9.wireOp",EDGE,"E28.1.5.0")])]});
            hole(context, id + "F17", {"style" : HoleStyle.C_BORE, "endStyle" : HoleEndStyle.BLIND, "holeDiameter" : 2 * mm, "cBoreDiameter" : 3 * mm, "cBoreDepth" : 0.6 * mm, "majorDiameter" : 5 * mm, "holeDepth" : 4.2 * mm, "isTappedThrough" : true, "tappedDepth" : 12 * mm, "tapClearance" : 3, "locations" : qUnion([Q0, Q1]), "scope" : qUnion([Q2])});
        }
        {
            var Q0;
            {var subQ0=sQuery(id+"F2.wireOp",EDGE,"E9");var subQ1=makeQuery(id+"F1.opExtrude","CAP_EDGE",EDGE,{"disambiguationData":[OSD([sQuery(id+"F0.wireOp",EDGE,"E1.3")])],"isStart":false});var subQ2=makeQuery(id+"F2.imprint","INTERSECT",VERTEX,{"disambiguationData":[OD(0.0)],"derivedFrom":[subQ1,subQ0]});Q0=makeQuery(id+"F2.imprint","IMPRINT",FACE,{"disambiguationData":[TD([[makeQuery(id+"F2.imprint","IMPRINT",EDGE,{"disambiguationData":[TD([[subQ2,1.0]])],"derivedFrom":subQ0}),1.0]])]});}
            var Q1;
            {var subQ0=sQuery(id+"F2.wireOp",EDGE,"E10");var subQ1=makeQuery(id+"F1.opExtrude","CAP_EDGE",EDGE,{"disambiguationData":[OSD([sQuery(id+"F0.wireOp",EDGE,"E1.1")])],"isStart":false});var subQ2=makeQuery(id+"F2.imprint","INTERSECT",VERTEX,{"disambiguationData":[OD(0.0)],"derivedFrom":[subQ1,subQ0]});Q1=makeQuery(id+"F2.imprint","IMPRINT",FACE,{"disambiguationData":[TD([[makeQuery(id+"F2.imprint","IMPRINT",EDGE,{"disambiguationData":[TD([[subQ2,-1.0]])],"derivedFrom":subQ0}),1.0]])]});}
            extrude(context, id + "F18", {"entities" : qUnion([Q0, Q1]), "operationType" : NewBodyOperationType.REMOVE, "oppositeDirection" : true, "depth" : 25 * mm, "offsetDistance" : 25 * mm});
        }
        {
            var Q0;
            Q0=makeQuery(id+"F1.opExtrude","SWEPT_EDGE",EDGE,{"disambiguationData":[OSD([sQuery(id+"F0.wireOp",EDGE,"E0.bottom"),sQuery(id+"F0.wireOp",EDGE,"E0.right")])]});
            var Q1;
            Q1=makeQuery(id+"F3.opExtrude","SWEPT_EDGE",EDGE,{"disambiguationData":[OSD([sQuery(id+"F2.wireOp",EDGE,"E2.2"),sQuery(id+"F2.wireOp",EDGE,"E2.3")])]});
            var Q2;
            Q2=makeQuery(id+"F3.opExtrude","SWEPT_EDGE",EDGE,{"disambiguationData":[OSD([sQuery(id+"F2.wireOp",EDGE,"E2.1"),sQuery(id+"F2.wireOp",EDGE,"E2.2")])]});
            var Q3;
            Q3=makeQuery(id+"F1.opExtrude","SWEPT_EDGE",EDGE,{"disambiguationData":[OSD([sQuery(id+"F0.wireOp",EDGE,"E0.bottom"),sQuery(id+"F0.wireOp",EDGE,"E0.left")])]});
            var Q4;
            Q4=makeQuery(id+"F3.opExtrude","SWEPT_EDGE",EDGE,{"disambiguationData":[OSD([sQuery(id+"F2.wireOp",EDGE,"E2.0"),sQuery(id+"F2.wireOp",EDGE,"E2.1")])]});
            var Q5;
            Q5=makeQuery(id+"F1.opExtrude","SWEPT_EDGE",EDGE,{"disambiguationData":[OSD([sQuery(id+"F0.wireOp",EDGE,"E0.top"),sQuery(id+"F0.wireOp",EDGE,"E0.left")])]});
            var Q6;
            Q6=makeQuery(id+"F3.opExtrude","SWEPT_EDGE",EDGE,{"disambiguationData":[OSD([sQuery(id+"F2.wireOp",EDGE,"E2.0"),sQuery(id+"F2.wireOp",EDGE,"E4.trimOffspring")])]});
            var Q7;
            Q7=makeQuery(id+"F1.opExtrude","SWEPT_EDGE",EDGE,{"disambiguationData":[OSD([sQuery(id+"F0.wireOp",EDGE,"E0.top"),sQuery(id+"F0.wireOp",EDGE,"E0.right")])]});
            fillet(context, id + "F19", {"entities" : qUnion([Q0, Q1, Q2, Q3, Q4, Q5, Q6, Q7]), "radius" : 1 * mm, "tangentPropagation" : true, "allowEdgeOverflow" : false});
        }
        {
            var Q0;
            Q0=makeQuery(id+"F7.imprint","IMPRINT",FACE,{"disambiguationData":[TD([[makeQuery(id+"F7.imprint","IMPRINT",EDGE,{"derivedFrom":sQuery(id+"F7.wireOp",EDGE,"E15")}),-1.0]])]});
            var sketch = newSketch(context, id + "F20", { "sketchPlane" : qUnion([Q0])});
            skCircle(sketch, "E46", {"center": v(-7, -5) * mm, "radius": 0.5 * mm});
            skCircle(sketch, "E47", {"center": v(7, -5) * mm, "radius": 0.5 * mm});
            skCircle(sketch, "E48", {"center": v(7, 5) * mm, "radius": 0.5 * mm});
            skCircle(sketch, "E49", {"center": v(-7, 5) * mm, "radius": 0.5 * mm});
            skSolve(sketch);
        }
        {
            var Q0;
            Q0 = qSketchRegion(id + "F20", true);
            var Q1;
            Q1=sQuery(id+"F20.wireOp",EDGE,"E46");
            var Q2;
            Q2=sQuery(id+"F20.wireOp",EDGE,"E47");
            var Q3;
            Q3=sQuery(id+"F20.wireOp",EDGE,"E48");
            var Q4;
            Q4=sQuery(id+"F20.wireOp",EDGE,"E49");
            extrude(context, id + "F21", {"entities" : qUnion([Q0]), "operationType" : NewBodyOperationType.ADD, "surfaceOperationType" : NewSurfaceOperationType.ADD, "surfaceEntities" : qUnion([Q1, Q2, Q3, Q4]), "oppositeDirection" : true, "depth" : 3.5 * mm, "offsetDistance" : 25 * mm});
        }
    });
